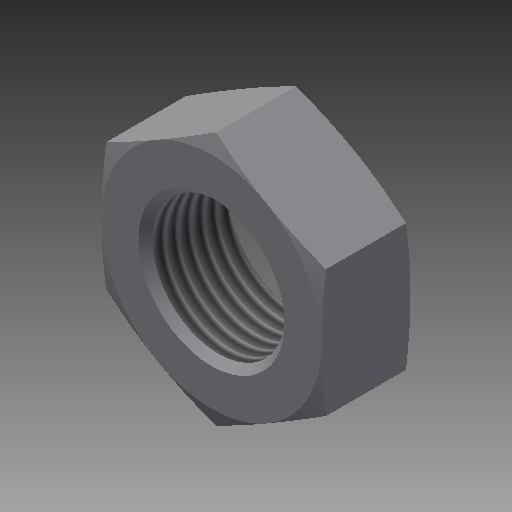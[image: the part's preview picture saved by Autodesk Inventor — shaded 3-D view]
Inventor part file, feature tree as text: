
AUTODESK INVENTOR PART (.ipt)
format: ipt  version: 2019 (Build 230136000, 136)  size: 184,320 bytes
history: native  units: in
note: dims shown in document units (in); Inventor stores cm internally (conversion verified against a paired STEP export)
features: other x70, sketch x3, revolve x2, extrude x1, thread x1
ambient origin geometry x8: Origin, YZ Plane, XZ Plane, XY Plane, X Axis, Y Axis, Z Axis, Center Point
bodies: Solid1 (feature_tree)
feature tree (77):
  sketch  "Sketch_8"  dims[d0=360.0deg d1=0.38in d2=0.0in]
  sketch  "Sketch_10"  dims[d3=360.0deg d4=0.3199in d5=0.0in]
  revolve  "Revolution1"  [1 undecoded]
  extrude  "Extrusion1"  Depth=0.3199in TaperAngle=0.0deg
  revolve  "Revolution2"  [1 undecoded]
  thread  "Thread1"  [1 undecoded]
  other  "NUT_XY"
  other  "NUT_YZ"
  other  "NUT_ZX"
  other  "NUT_X"
  other  "NUT_Y"
  other  "NUT_Z"
  other  "NUT_Center"
  other  "a1_XY"
  other  "a1_YZ"
  other  "a1_ZX"
  other  "a1_X"
  other  "a1_Y"
  other  "a1_Z"
  other  "a1_Center"
  other  "a2_XY"
  other  "a2_YZ"
  other  "a2_ZX"
  other  "a2_X"
  other  "a2_Y"
  other  "a2_Z"
  other  "a2_Center"
  other  "b1_XY"
  other  "b1_YZ"
  other  "b1_ZX"
  other  "b1_X"
  other  "b1_Y"
  other  "b1_Z"
  other  "b1_Center"
  other  "b2_XY"
  other  "b2_YZ"
  other  "b2_ZX"
  other  "b2_X"
  other  "b2_Y"
  other  "b2_Z"
  other  "b2_Center"
  other  "e_XY"
  other  "e_YZ"
  other  "e_ZX"
  other  "e_X"
  other  "e_Y"
  other  "e_Z"
  other  "e_Center"
  other  "ol1_XY"
  other  "ol1_YZ"
  other  "ol1_ZX"
  other  "ol1_X"
  other  "ol1_Y"
  other  "ol1_Z"
  other  "ol1_Center"
  other  "ol2_XY"
  other  "ol2_YZ"
  other  "ol2_ZX"
  other  "ol2_X"
  other  "ol2_Y"
  other  "ol2_Z"
  other  "ol2_Center"
  other  "th1_XY"
  other  "th1_YZ"
  other  "th1_ZX"
  other  "th1_X"
  other  "th1_Y"
  other  "th1_Z"
  other  "th1_Center"
  other  "th2_XY"
  other  "th2_YZ"
  other  "th2_ZX"
  other  "th2_X"
  other  "th2_Y"
  other  "th2_Z"
  other  "th2_Center"
  sketch  "Sketch_11"  dims[d6=0.0in d7=0.0in d8=0.0in]
note: 3 required parameter values undecoded (feature->parameter linkage not recoverable at this tier; creation-order binding heuristic only, values carry confidence <= 0.55)